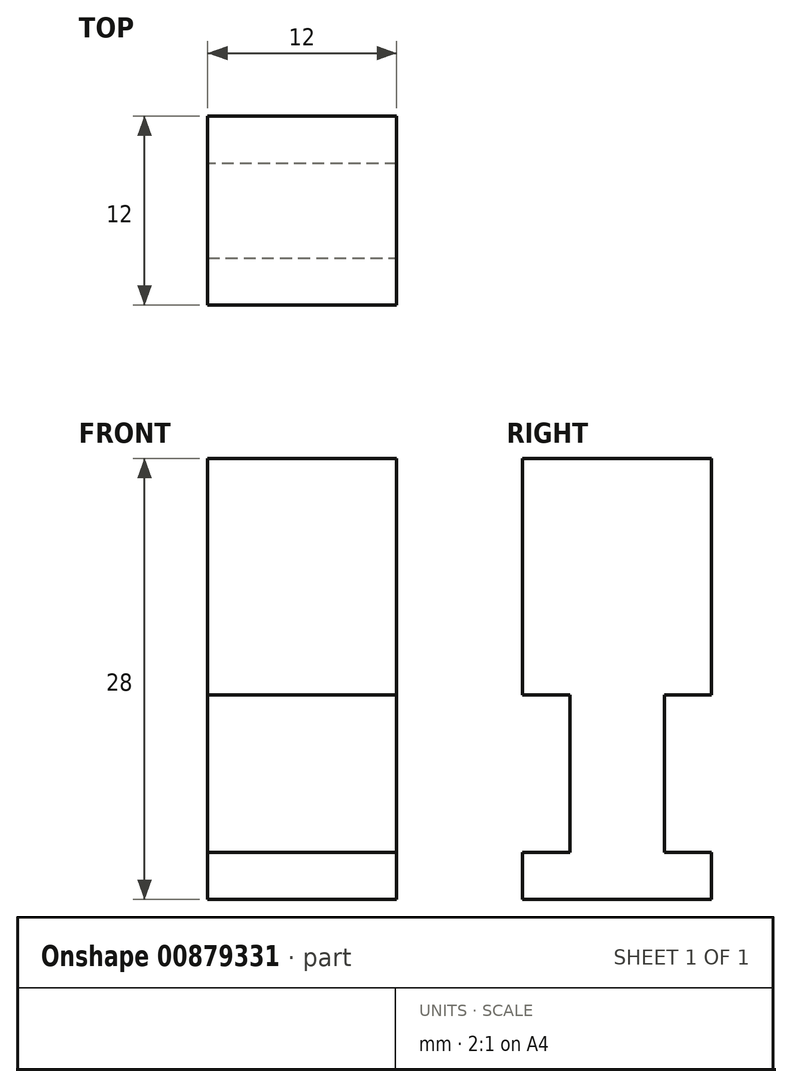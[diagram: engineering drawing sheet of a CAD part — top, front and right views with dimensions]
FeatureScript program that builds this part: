
annotation { "Feature Type Name" : "Feature", "Feature Type Description" : "" }
export const myFeature = defineFeature(function(context is Context, id is Id, definition is map)
    precondition{}
    {
        {
            var Q0;
            Q0=qCreatedBy(makeId("Top.planeOp"),FACE);
            var sketch = newSketch(context, id + "F0", { "sketchPlane" : qUnion([Q0])});
            skLineSegment(sketch, "E0.bottom", {"start": v(0, 0) * mm, "end": v(-12, 0) * mm});
            skLineSegment(sketch, "E0.top", {"start": v(0, 12) * mm, "end": v(-12, 12) * mm});
            skLineSegment(sketch, "E0.left", {"start": v(0, 0) * mm, "end": v(0, 12) * mm});
            skLineSegment(sketch, "E0.right", {"start": v(-12, 0) * mm, "end": v(-12, 12) * mm});
            skSolve(sketch);
        }
        {
            var Q0;
            Q0=makeQuery(id+"F0.imprint","IMPRINT",FACE,{"disambiguationData":[TD([[makeQuery(id+"F0.imprint","IMPRINT",EDGE,{"derivedFrom":sQuery(id+"F0.wireOp",EDGE,"E0.bottom")}),-1.0]])]});
            extrude(context, id + "F1", {"entities" : qUnion([Q0]), "depth" : 3 * mm, "offsetDistance" : 25 * mm});
        }
        {
            var Q0;
            Q0=makeQuery(id+"F1.opExtrude","CAP_FACE",FACE,{"disambiguationData":[OSD([sQuery(id+"F0.wireOp",EDGE,"E0.bottom"),sQuery(id+"F0.wireOp",EDGE,"E0.top"),sQuery(id+"F0.wireOp",EDGE,"E0.left"),sQuery(id+"F0.wireOp",EDGE,"E0.right")])],"isStart":false});
            var sketch = newSketch(context, id + "F2", { "sketchPlane" : qUnion([Q0])});
            skLineSegment(sketch, "E1", {"start": v(-12, 3) * mm, "end": v(0, 3) * mm});
            skLineSegment(sketch, "E2", {"start": v(0, 9) * mm, "end": v(-12, 9) * mm});
            skSolve(sketch);
        }
        {
            var Q0;
            {var subQ0=sQuery(id+"F2.wireOp",EDGE,"E1");Q0=makeQuery(id+"F2.imprint","IMPRINT",FACE,{"disambiguationData":[TD([[makeQuery(id+"F2.imprint","IMPRINT",EDGE,{"derivedFrom":subQ0}),1.0]])]});}
            extrude(context, id + "F3", {"entities" : qUnion([Q0]), "operationType" : NewBodyOperationType.ADD, "depth" : 10 * mm, "offsetDistance" : 25 * mm});
        }
        {
            var Q0;
            Q0=makeQuery(id+"F3.opExtrude","CAP_FACE",FACE,{"disambiguationData":[OSD([sQuery(id+"F0.wireOp",EDGE,"E0.left"),sQuery(id+"F0.wireOp",EDGE,"E0.right"),sQuery(id+"F2.wireOp",EDGE,"E1"),sQuery(id+"F2.wireOp",EDGE,"E2")])],"isStart":false});
            var sketch = newSketch(context, id + "F4", { "sketchPlane" : qUnion([Q0])});
            skLineSegment(sketch, "E3", {"start": v(-12, 3) * mm, "end": v(-12, 0) * mm});
            skLineSegment(sketch, "E4", {"start": v(-12, 0) * mm, "end": v(0, 0) * mm});
            skLineSegment(sketch, "E5", {"start": v(0, 0) * mm, "end": v(0, 3) * mm});
            skLineSegment(sketch, "E6", {"start": v(0, 9) * mm, "end": v(0, 12) * mm});
            skLineSegment(sketch, "E7", {"start": v(0, 12) * mm, "end": v(-12, 12) * mm});
            skLineSegment(sketch, "E8", {"start": v(-12, 12) * mm, "end": v(-12, 9) * mm});
            skSolve(sketch);
        }
        {
            var Q0;
            Q0=makeQuery(id+"F4.imprint","IMPRINT",FACE,{"disambiguationData":[TD([[makeQuery(id+"F4.imprint","IMPRINT",EDGE,{"derivedFrom":sQuery(id+"F4.wireOp",EDGE,"E3")}),1.0]])]});
            var Q1;
            Q1=makeQuery(id+"F4.imprint","IMPRINT",FACE,{"disambiguationData":[TD([[makeQuery(id+"F4.imprint","IMPRINT",EDGE,{"derivedFrom":makeQuery(id+"F3.opExtrude","CAP_EDGE",EDGE,{"disambiguationData":[OSD([sQuery(id+"F2.wireOp",EDGE,"E1")])],"isStart":false})}),1.0]])]});
            var Q2;
            Q2=makeQuery(id+"F4.imprint","IMPRINT",FACE,{"disambiguationData":[TD([[makeQuery(id+"F4.imprint","IMPRINT",EDGE,{"derivedFrom":sQuery(id+"F4.wireOp",EDGE,"E6")}),1.0]])]});
            extrude(context, id + "F5", {"entities" : qUnion([Q0, Q1, Q2]), "operationType" : NewBodyOperationType.ADD, "depth" : 15 * mm, "offsetDistance" : 25 * mm});
        }
    });
